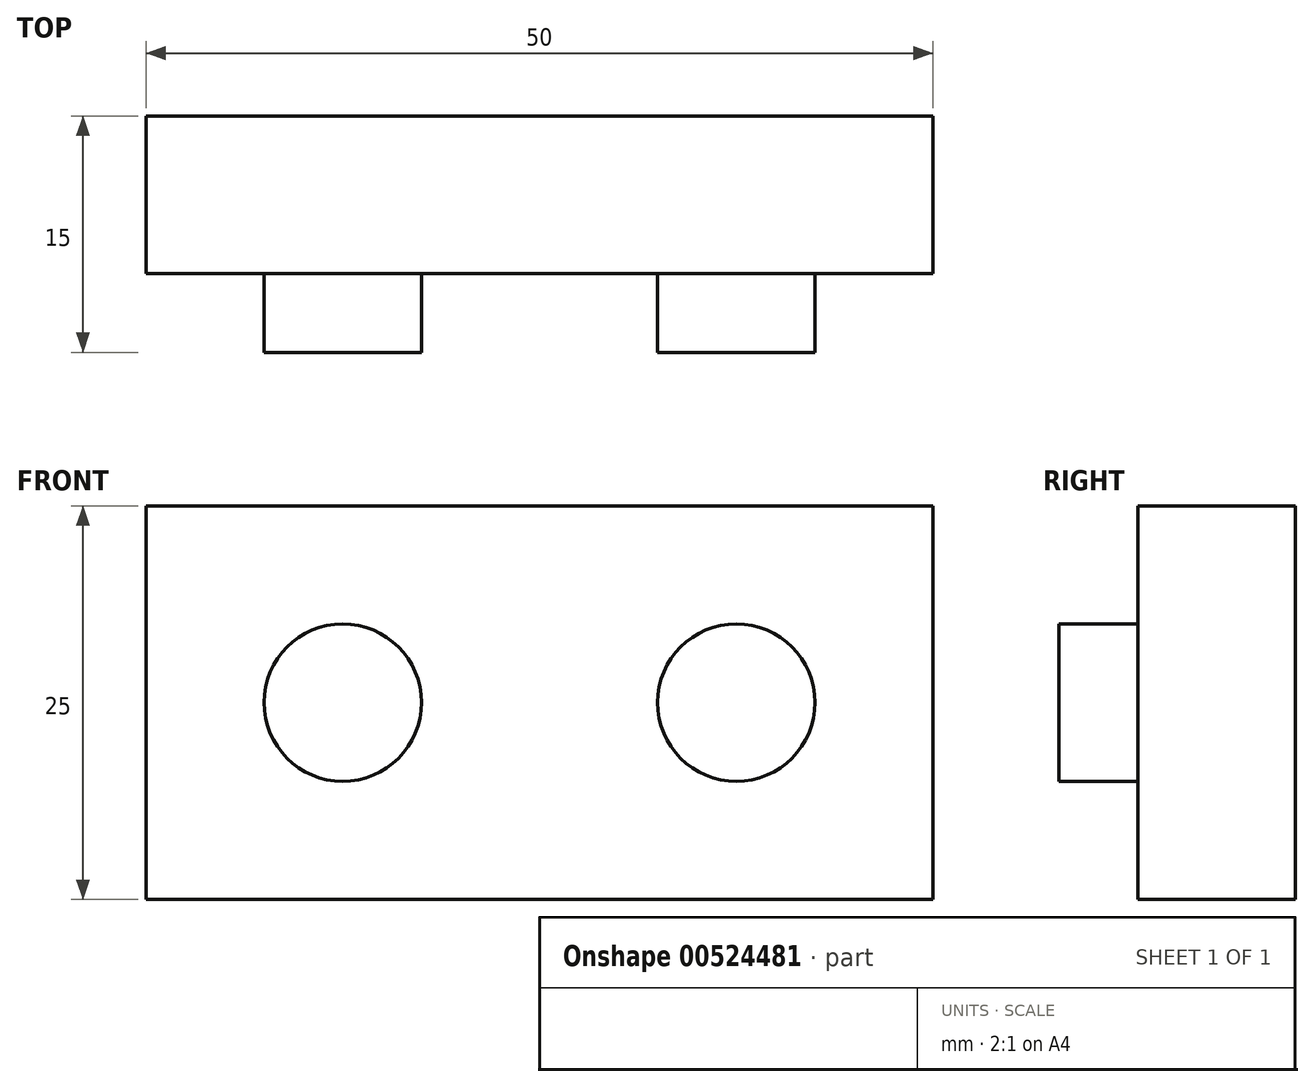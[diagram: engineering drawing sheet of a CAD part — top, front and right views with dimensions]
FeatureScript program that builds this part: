
annotation { "Feature Type Name" : "Feature", "Feature Type Description" : "" }
export const myFeature = defineFeature(function(context is Context, id is Id, definition is map)
    precondition{}
    {
        {
            var Q0;
            Q0=qCreatedBy(makeId("Front.planeOp"),FACE);
            var sketch = newSketch(context, id + "F0", { "sketchPlane" : qUnion([Q0])});
            skLineSegment(sketch, "E0.bottom", {"start": v(25, -12.5) * mm, "end": v(-25, -12.5) * mm});
            skLineSegment(sketch, "E0.top", {"start": v(25, 12.5) * mm, "end": v(-25, 12.5) * mm});
            skLineSegment(sketch, "E0.left", {"start": v(25, -12.5) * mm, "end": v(25, 12.5) * mm});
            skLineSegment(sketch, "E0.right", {"start": v(-25, -12.5) * mm, "end": v(-25, 12.5) * mm});
            skPoint(sketch, "E0.middle", {"position": v(0, 0) * mm});
            skSolve(sketch);
        }
        {
            var Q0;
            Q0 = qSketchRegion(id + "F0", true);
            extrude(context, id + "F1", {"entities" : qUnion([Q0]), "depth" : 10 * mm, "offsetDistance" : 25 * mm});
        }
        {
            var Q0;
            Q0=makeQuery(id+"F1.opExtrude","CAP_FACE",FACE,{"disambiguationData":[OSD([sQuery(id+"F0.wireOp",EDGE,"E0.bottom"),sQuery(id+"F0.wireOp",EDGE,"E0.top"),sQuery(id+"F0.wireOp",EDGE,"E0.left"),sQuery(id+"F0.wireOp",EDGE,"E0.right")])],"isStart":false});
            var sketch = newSketch(context, id + "F2", { "sketchPlane" : qUnion([Q0])});
            skLineSegment(sketch, "E1", {"start": v(0, 0) * mm, "end": v(25, 0) * mm, "construction": true});
            skLineSegment(sketch, "E2", {"start": v(0, 0) * mm, "end": v(-25, 0) * mm, "construction": true});
            skLineSegment(sketch, "E3", {"start": v(-12.5, 0) * mm, "end": v(-12.5, -12.5) * mm, "construction": true});
            skLineSegment(sketch, "E4", {"start": v(12.5, 0) * mm, "end": v(12.5, -12.5) * mm, "construction": true});
            skLineSegment(sketch, "E5", {"start": v(12.5, 0) * mm, "end": v(12.5, 12.5) * mm, "construction": true});
            skLineSegment(sketch, "E6", {"start": v(-12.5, 0) * mm, "end": v(-12.5, 12.5) * mm, "construction": true});
            skCircle(sketch, "E7", {"center": v(-12.5, 0) * mm, "radius": 5 * mm});
            skCircle(sketch, "E8", {"center": v(12.5, 0) * mm, "radius": 5 * mm});
            skSolve(sketch);
        }
        {
            var Q0;
            Q0 = qSketchRegion(id + "F2", true);
            extrude(context, id + "F3", {"entities" : qUnion([Q0]), "operationType" : NewBodyOperationType.ADD, "depth" : 5 * mm, "offsetDistance" : 25 * mm});
        }
    });
